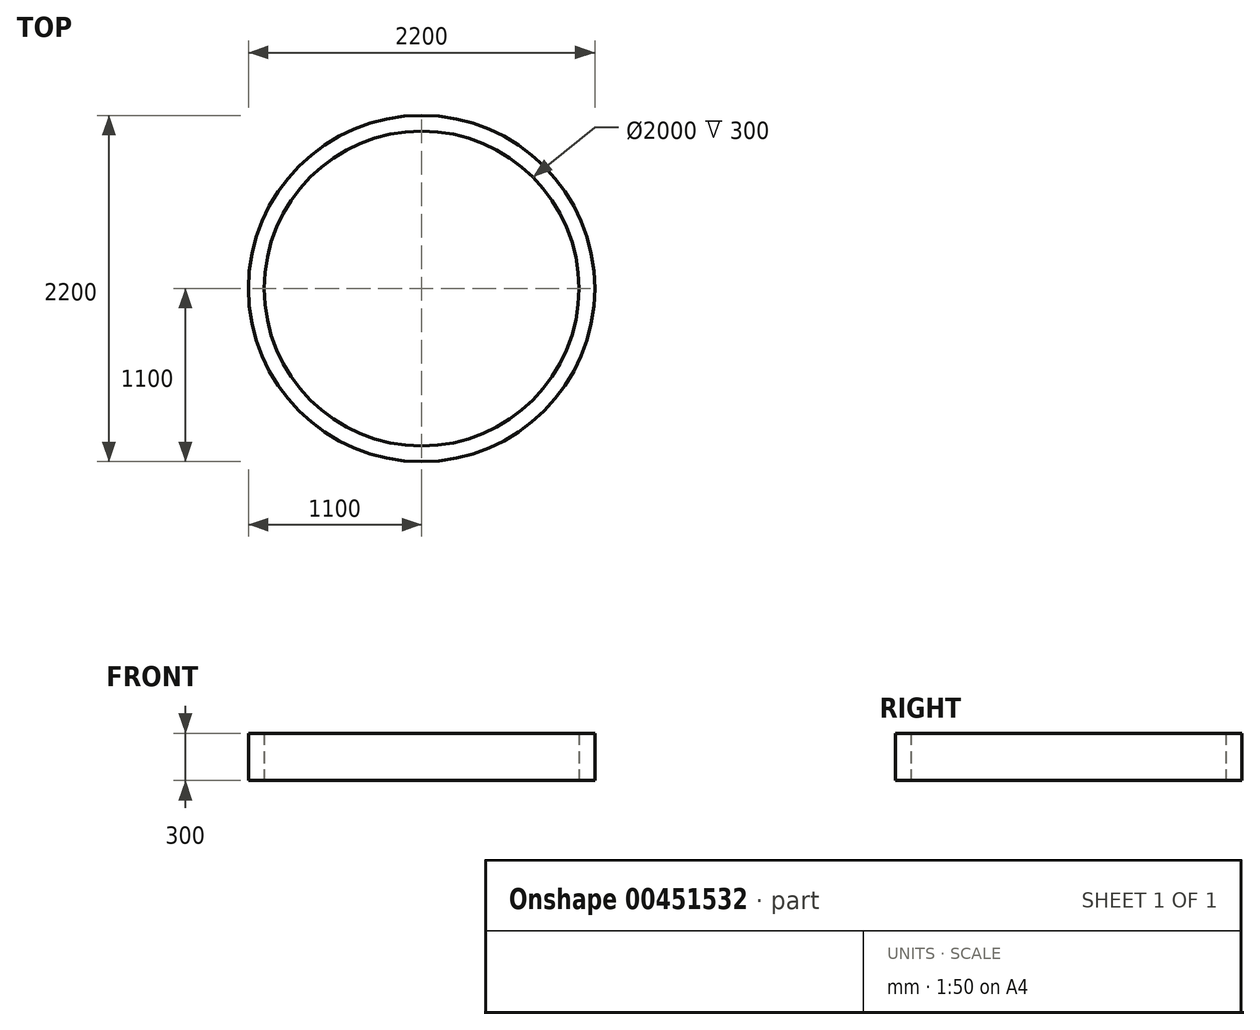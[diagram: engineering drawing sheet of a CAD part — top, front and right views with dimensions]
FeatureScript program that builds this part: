
annotation { "Feature Type Name" : "Feature", "Feature Type Description" : "" }
export const myFeature = defineFeature(function(context is Context, id is Id, definition is map)
    precondition{}
    {
        {
            var Q0;
            Q0=qCreatedBy(makeId("Top.planeOp"),FACE);
            var sketch = newSketch(context, id + "F0", { "sketchPlane" : qUnion([Q0])});
            skCircle(sketch, "E0", {"center": v(0, 0) * mm, "radius": 1100 * mm});
            skCircle(sketch, "E1", {"center": v(0, 0) * mm, "radius": 1000 * mm});
            skSolve(sketch);
        }
        {
            var Q0;
            Q0 = qSketchRegion(id + "F0", true);
            extrude(context, id + "F1", {"entities" : qUnion([Q0]), "endBound" : BoundingType.SYMMETRIC, "depth" : 300 * mm});
        }
    });
